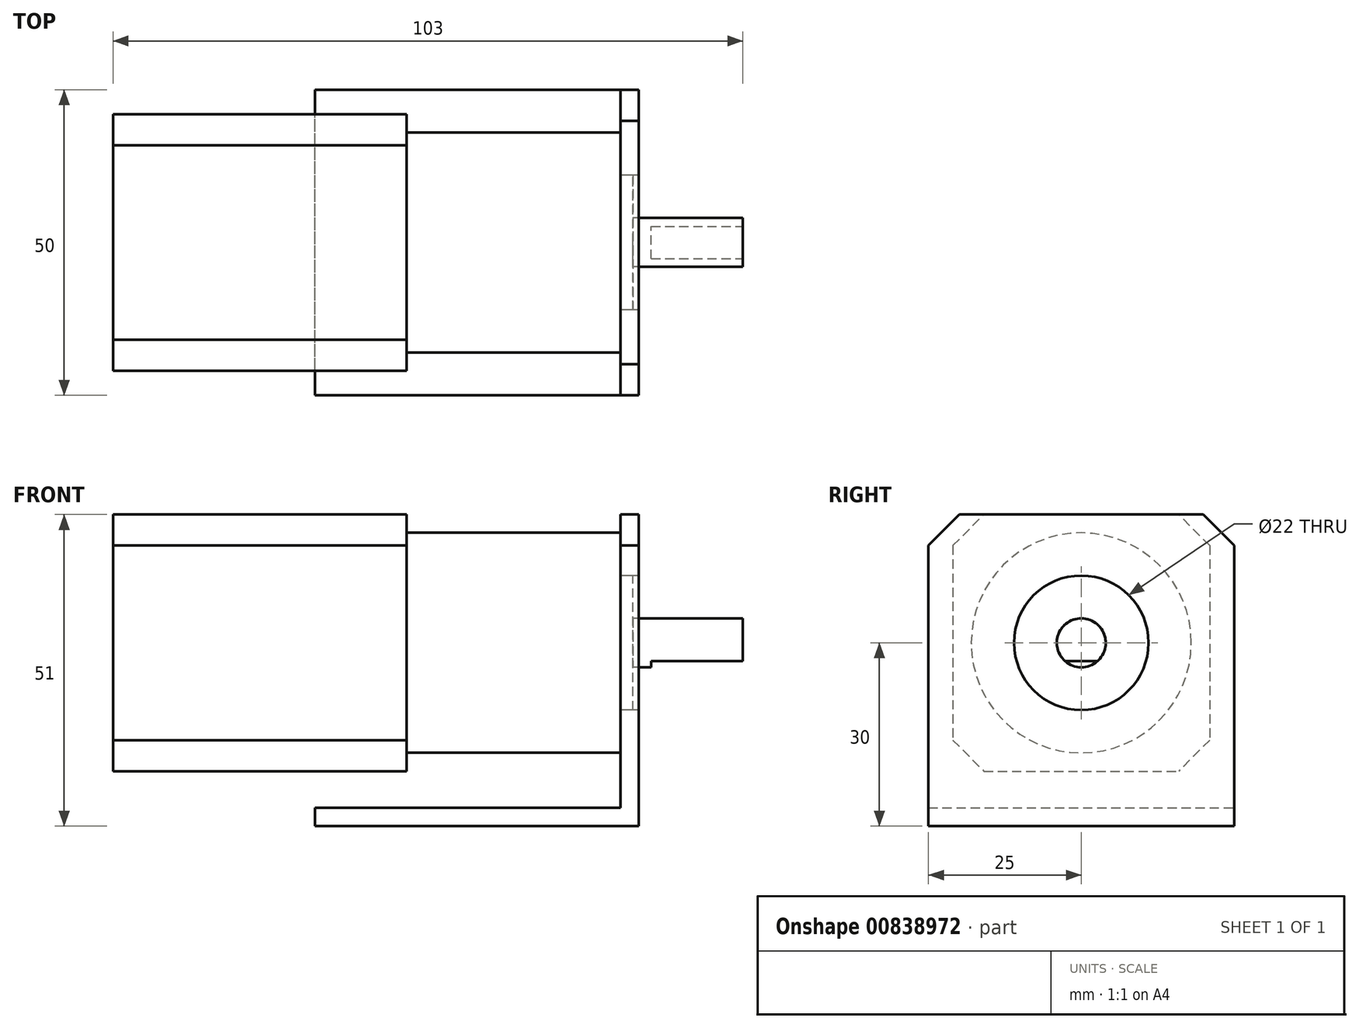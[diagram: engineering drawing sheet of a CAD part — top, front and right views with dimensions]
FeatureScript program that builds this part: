
annotation { "Feature Type Name" : "Feature", "Feature Type Description" : "" }
export const myFeature = defineFeature(function(context is Context, id is Id, definition is map)
    precondition{}
    {
        {
            var Q0;
            Q0=qCreatedBy(makeId("Right.planeOp"),FACE);
            var sketch = newSketch(context, id + "F0", { "sketchPlane" : qUnion([Q0])});
            skCircle(sketch, "E0", {"center": v(0, 0) * mm, "radius": 18 * mm});
            skSolve(sketch);
        }
        {
            var Q0;
            Q0 = qSketchRegion(id + "F0", true);
            extrude(context, id + "F1", {"entities" : qUnion([Q0]), "depth" : 35 * mm, "offsetDistance" : 25.4 * mm});
        }
        {
            var Q0;
            Q0=makeQuery(id+"F1.opExtrude","CAP_FACE",FACE,{"disambiguationData":[OSD([sQuery(id+"F0.wireOp",EDGE,"E0")])],"isStart":true});
            var sketch = newSketch(context, id + "F2", { "sketchPlane" : qUnion([Q0])});
            skLineSegment(sketch, "E1.bottom", {"start": v(21, 21) * mm, "end": v(-21, 21) * mm});
            skLineSegment(sketch, "E1.top", {"start": v(21, -21) * mm, "end": v(-21, -21) * mm});
            skLineSegment(sketch, "E1.left", {"start": v(21, 21) * mm, "end": v(21, -21) * mm});
            skLineSegment(sketch, "E1.right", {"start": v(-21, 21) * mm, "end": v(-21, -21) * mm});
            skPoint(sketch, "E1.middle", {"position": v(0, 0) * mm});
            skSolve(sketch);
        }
        {
            var Q0;
            Q0 = qSketchRegion(id + "F2", true);
            extrude(context, id + "F3", {"entities" : qUnion([Q0]), "operationType" : NewBodyOperationType.ADD, "depth" : 48 * mm, "offsetDistance" : 25.4 * mm});
        }
        {
            var Q0;
            Q0=makeQuery(id+"F3.opExtrude","SWEPT_EDGE",EDGE,{"disambiguationData":[OSD([sQuery(id+"F2.wireOp",EDGE,"E1.bottom"),sQuery(id+"F2.wireOp",EDGE,"E1.left")])]});
            var Q1;
            Q1=makeQuery(id+"F3.opExtrude","SWEPT_EDGE",EDGE,{"disambiguationData":[OSD([sQuery(id+"F2.wireOp",EDGE,"E1.bottom"),sQuery(id+"F2.wireOp",EDGE,"E1.right")])]});
            var Q2;
            Q2=makeQuery(id+"F3.opExtrude","SWEPT_EDGE",EDGE,{"disambiguationData":[OSD([sQuery(id+"F2.wireOp",EDGE,"E1.top"),sQuery(id+"F2.wireOp",EDGE,"E1.right")])]});
            var Q3;
            Q3=makeQuery(id+"F3.opExtrude","SWEPT_EDGE",EDGE,{"disambiguationData":[OSD([sQuery(id+"F2.wireOp",EDGE,"E1.top"),sQuery(id+"F2.wireOp",EDGE,"E1.left")])]});
            chamfer(context, id + "F4", {"entities" : qUnion([Q0, Q1, Q2, Q3]), "width" : 5.08 * mm, "tangentPropagation" : true});
        }
        {
            var Q0;
            Q0=makeQuery(id+"F1.opExtrude","CAP_FACE",FACE,{"disambiguationData":[OSD([sQuery(id+"F0.wireOp",EDGE,"E0")])],"isStart":false});
            var sketch = newSketch(context, id + "F5", { "sketchPlane" : qUnion([Q0])});
            skCircle(sketch, "E2", {"center": v(0, 0) * mm, "radius": 11 * mm});
            skSolve(sketch);
        }
        {
            var Q0;
            Q0 = qSketchRegion(id + "F5", true);
            extrude(context, id + "F6", {"entities" : qUnion([Q0]), "operationType" : NewBodyOperationType.ADD, "depth" : 2 * mm, "offsetDistance" : 25.4 * mm});
        }
        {
            var Q0;
            Q0=makeQuery(id+"F6.opExtrude","CAP_FACE",FACE,{"disambiguationData":[OSD([sQuery(id+"F5.wireOp",EDGE,"E2")])],"isStart":false});
            var sketch = newSketch(context, id + "F7", { "sketchPlane" : qUnion([Q0])});
            skCircle(sketch, "E3", {"center": v(0, 0) * mm, "radius": 4 * mm});
            skSolve(sketch);
        }
        {
            var Q0;
            Q0 = qSketchRegion(id + "F7", true);
            extrude(context, id + "F8", {"entities" : qUnion([Q0]), "operationType" : NewBodyOperationType.ADD, "depth" : 18 * mm, "offsetDistance" : 25.4 * mm});
        }
        {
            var Q0;
            Q0=makeQuery(id+"F8.opExtrude","CAP_FACE",FACE,{"disambiguationData":[OSD([sQuery(id+"F7.wireOp",EDGE,"E3")])],"isStart":false});
            var sketch = newSketch(context, id + "F9", { "sketchPlane" : qUnion([Q0])});
            skLineSegment(sketch, "E4", {"start": v(-2.65, -3) * mm, "end": v(2.65, -3) * mm});
            skArc(sketch, "E5", {"start": v(-2.65, -3) * mm, "mid": v(0, -4) * mm, "end": v(2.65, -3) * mm});
            skSolve(sketch);
        }
        {
            var Q0;
            Q0 = qSketchRegion(id + "F9", true);
            extrude(context, id + "F10", {"entities" : qUnion([Q0]), "operationType" : NewBodyOperationType.REMOVE, "oppositeDirection" : true, "depth" : 15 * mm, "offsetDistance" : 25.4 * mm});
        }
        {
            var Q0;
            Q0=makeQuery(id+"F1.opExtrude","CAP_FACE",FACE,{"disambiguationData":[OSD([sQuery(id+"F0.wireOp",EDGE,"E0")])],"isStart":false});
            var sketch = newSketch(context, id + "F11", { "sketchPlane" : qUnion([Q0])});
            skCircle(sketch, "E6", {"center": v(0, 0) * mm, "radius": 11 * mm});
            skLineSegment(sketch, "E7.bottom", {"start": v(-25, 21) * mm, "end": v(25, 21) * mm});
            skLineSegment(sketch, "E7.top", {"start": v(-25, -30) * mm, "end": v(25, -30) * mm});
            skLineSegment(sketch, "E7.left", {"start": v(-25, 21) * mm, "end": v(-25, -30) * mm});
            skLineSegment(sketch, "E7.right", {"start": v(25, 21) * mm, "end": v(25, -30) * mm});
            skSolve(sketch);
        }
        {
            var Q0;
            Q0 = qSketchRegion(id + "F11", true);
            extrude(context, id + "F12", {"entities" : qUnion([Q0]), "depth" : 3 * mm, "offsetDistance" : 25.4 * mm});
        }
        {
            var Q0;
            Q0=makeQuery(id+"F12.opExtrude","SWEPT_EDGE",EDGE,{"disambiguationData":[OSD([sQuery(id+"F11.wireOp",EDGE,"E7.bottom"),sQuery(id+"F11.wireOp",EDGE,"E7.left")])]});
            var Q1;
            Q1=makeQuery(id+"F12.opExtrude","SWEPT_EDGE",EDGE,{"disambiguationData":[OSD([sQuery(id+"F11.wireOp",EDGE,"E7.bottom"),sQuery(id+"F11.wireOp",EDGE,"E7.right")])]});
            chamfer(context, id + "F13", {"entities" : qUnion([Q0, Q1]), "width" : 5.08 * mm, "tangentPropagation" : true});
        }
        {
            var Q0;
            Q0=makeQuery(id+"F12.opExtrude","SWEPT_FACE",FACE,{"disambiguationData":[OSD([sQuery(id+"F11.wireOp",EDGE,"E7.top")])]});
            var sketch = newSketch(context, id + "F14", { "sketchPlane" : qUnion([Q0])});
            skLineSegment(sketch, "E8.bottom", {"start": v(35, 25) * mm, "end": v(-15, 25) * mm});
            skLineSegment(sketch, "E8.top", {"start": v(35, -25) * mm, "end": v(-15, -25) * mm});
            skLineSegment(sketch, "E8.left", {"start": v(35, 25) * mm, "end": v(35, -25) * mm});
            skLineSegment(sketch, "E8.right", {"start": v(-15, 25) * mm, "end": v(-15, -25) * mm});
            skSolve(sketch);
        }
        {
            var Q0;
            Q0 = qSketchRegion(id + "F14", true);
            extrude(context, id + "F15", {"entities" : qUnion([Q0]), "operationType" : NewBodyOperationType.ADD, "oppositeDirection" : true, "depth" : 3 * mm, "offsetDistance" : 25.4 * mm});
        }
    });
